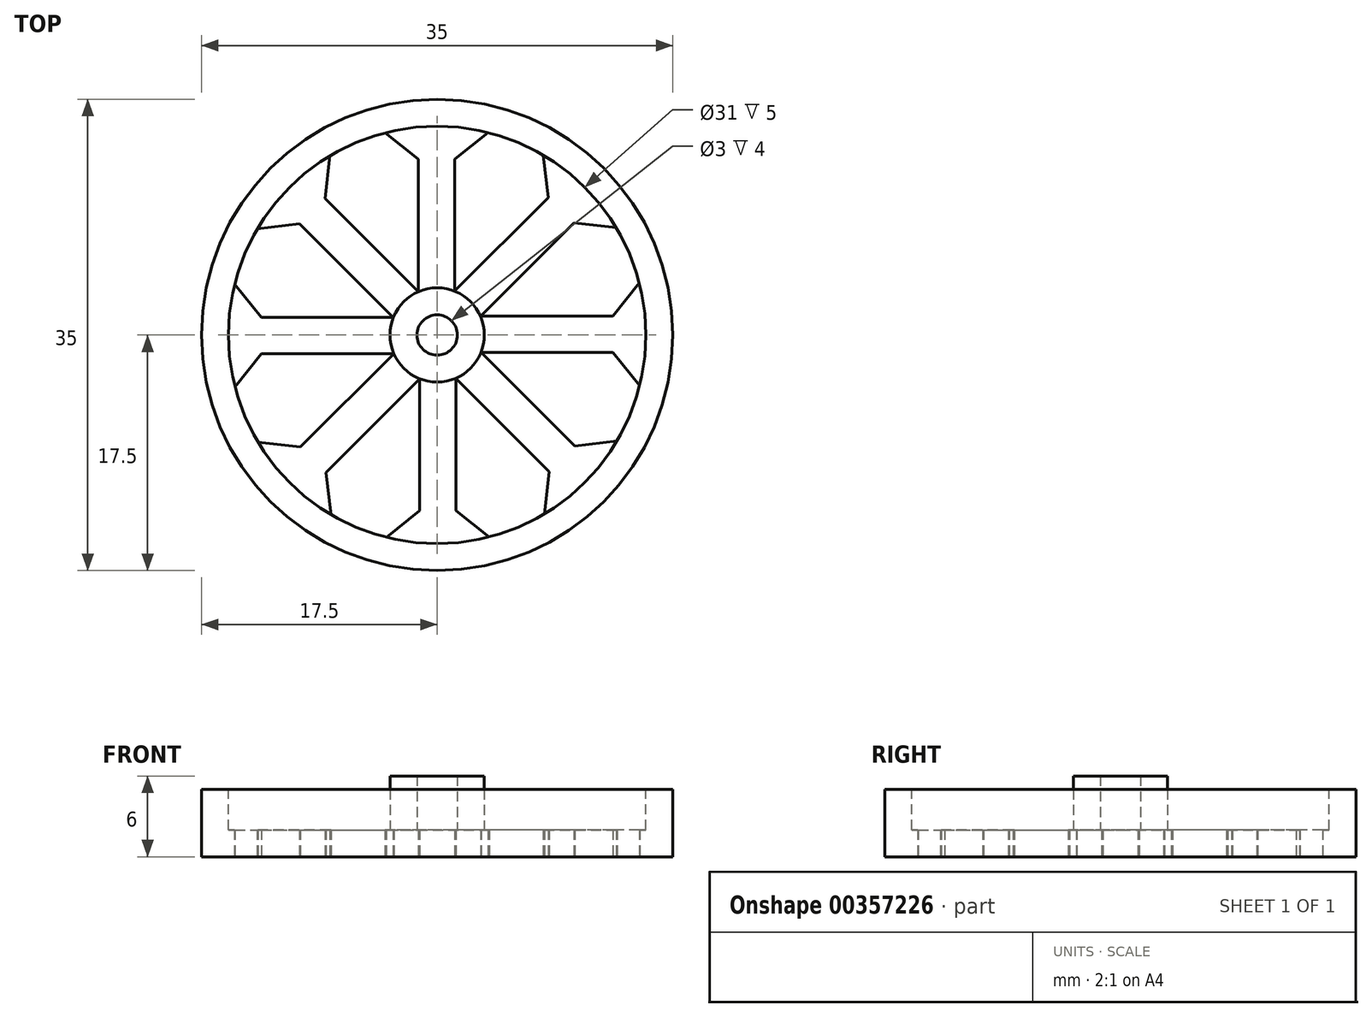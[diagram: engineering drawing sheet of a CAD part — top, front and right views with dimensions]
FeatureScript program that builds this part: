
annotation { "Feature Type Name" : "Feature", "Feature Type Description" : "" }
export const myFeature = defineFeature(function(context is Context, id is Id, definition is map)
    precondition{}
    {
        {
            var Q0;
            Q0=qCreatedBy(makeId("Top.planeOp"),FACE);
            var sketch = newSketch(context, id + "F0", { "sketchPlane" : qUnion([Q0])});
            skCircle(sketch, "E0", {"center": v(0, 0) * mm, "radius": 17.5 * mm});
            skSolve(sketch);
        }
        {
            var Q0;
            Q0=makeQuery(id+"F0.imprint","IMPRINT",FACE,{"disambiguationData":[TD([[makeQuery(id+"F0.imprint","IMPRINT",EDGE,{"derivedFrom":sQuery(id+"F0.wireOp",EDGE,"E0")}),1.0]])]});
            extrude(context, id + "F1", {"entities" : qUnion([Q0]), "depth" : 5 * mm});
        }
        {
            var Q0;
            Q0=makeQuery(id+"F1.opExtrude","CAP_FACE",FACE,{"disambiguationData":[OSD([sQuery(id+"F0.wireOp",EDGE,"E0")])],"isStart":false});
            var sketch = newSketch(context, id + "F2", { "sketchPlane" : qUnion([Q0])});
            skCircle(sketch, "E1", {"center": v(0, 0) * mm, "radius": 15.5 * mm});
            skSolve(sketch);
        }
        {
            var Q0;
            Q0 = qSketchRegion(id + "F2", true);
            extrude(context, id + "F3", {"entities" : qUnion([Q0]), "operationType" : NewBodyOperationType.REMOVE, "oppositeDirection" : true, "depth" : 3 * mm});
        }
        {
            var Q0;
            Q0=qCreatedBy(makeId("Top.planeOp"),FACE);
            var sketch = newSketch(context, id + "F4", { "sketchPlane" : qUnion([Q0])});
            skCircle(sketch, "E2", {"center": v(0, 0) * mm, "radius": 1.5 * mm});
            skCircle(sketch, "E3", {"center": v(0, 0) * mm, "radius": 3.5 * mm});
            skSolve(sketch);
        }
        {
            var Q0;
            Q0 = qSketchRegion(id + "F4", true);
            extrude(context, id + "F5", {"entities" : qUnion([Q0]), "operationType" : NewBodyOperationType.ADD, "depth" : 6 * mm});
        }
        {
            var Q0;
            Q0=makeQuery(id+"F1.opExtrude","CAP_FACE",FACE,{"disambiguationData":[OSD([sQuery(id+"F0.wireOp",EDGE,"E0")])],"isStart":true});
            var sketch = newSketch(context, id + "F6", { "sketchPlane" : qUnion([Q0])});
            skCircle(sketch, "E4", {"center": v(0, 0) * mm, "radius": 15.5 * mm});
            skSolve(sketch);
        }
        {
            var Q0;
            Q0=makeQuery(id+"F6.imprint","IMPRINT",FACE,{"disambiguationData":[TD([[makeQuery(id+"F6.imprint","IMPRINT",EDGE,{"derivedFrom":sQuery(id+"F6.wireOp",EDGE,"E4")}),1.0]])]});
            var sketch = newSketch(context, id + "F7", { "sketchPlane" : qUnion([Q0])});
            skLineSegment(sketch, "E5", {"start": v(-1.3, 2.05) * mm, "end": v(-1.3, 13.05) * mm});
            skLineSegment(sketch, "E6", {"start": v(1.39, 2.05) * mm, "end": v(1.39, 13.05) * mm});
            skLineSegment(sketch, "E7", {"start": v(1.39, 13.05) * mm, "end": v(4.83, 15.76) * mm});
            skLineSegment(sketch, "E8", {"start": v(-1.3, 13.05) * mm, "end": v(-4.67, 15.76) * mm});
            skLineSegment(sketch, "E9.1.0", {"start": v(-2.37, 0.53) * mm, "end": v(-10.15, 8.3) * mm});
            skLineSegment(sketch, "E9.1.1", {"start": v(-10.15, 8.3) * mm, "end": v(-14.45, 7.84) * mm});
            skLineSegment(sketch, "E9.1.2", {"start": v(-8.25, 10.2) * mm, "end": v(-7.72, 14.56) * mm});
            skLineSegment(sketch, "E9.1.3", {"start": v(-0.47, 2.43) * mm, "end": v(-8.25, 10.2) * mm});
            skLineSegment(sketch, "E9.2.0", {"start": v(-2.05, -1.3) * mm, "end": v(-13.05, -1.3) * mm});
            skLineSegment(sketch, "E9.2.1", {"start": v(-13.05, -1.3) * mm, "end": v(-15.76, -4.67) * mm});
            skLineSegment(sketch, "E9.2.2", {"start": v(-13.05, 1.39) * mm, "end": v(-15.76, 4.83) * mm});
            skLineSegment(sketch, "E9.2.3", {"start": v(-2.05, 1.39) * mm, "end": v(-13.05, 1.39) * mm});
            skLineSegment(sketch, "E9.3.0", {"start": v(-0.53, -2.37) * mm, "end": v(-8.3, -10.15) * mm});
            skLineSegment(sketch, "E9.3.1", {"start": v(-8.3, -10.15) * mm, "end": v(-7.84, -14.45) * mm});
            skLineSegment(sketch, "E9.3.2", {"start": v(-10.2, -8.25) * mm, "end": v(-14.56, -7.72) * mm});
            skLineSegment(sketch, "E9.3.3", {"start": v(-2.43, -0.47) * mm, "end": v(-10.2, -8.25) * mm});
            skLineSegment(sketch, "E9.4.0", {"start": v(1.3, -2.05) * mm, "end": v(1.3, -13.05) * mm});
            skLineSegment(sketch, "E9.4.1", {"start": v(1.3, -13.05) * mm, "end": v(4.67, -15.76) * mm});
            skLineSegment(sketch, "E9.4.2", {"start": v(-1.39, -13.05) * mm, "end": v(-4.83, -15.76) * mm});
            skLineSegment(sketch, "E9.4.3", {"start": v(-1.39, -2.05) * mm, "end": v(-1.39, -13.05) * mm});
            skLineSegment(sketch, "E9.5.0", {"start": v(2.37, -0.53) * mm, "end": v(10.15, -8.3) * mm});
            skLineSegment(sketch, "E9.5.1", {"start": v(10.15, -8.3) * mm, "end": v(14.45, -7.84) * mm});
            skLineSegment(sketch, "E9.5.2", {"start": v(8.25, -10.2) * mm, "end": v(7.72, -14.56) * mm});
            skLineSegment(sketch, "E9.5.3", {"start": v(0.47, -2.43) * mm, "end": v(8.25, -10.2) * mm});
            skLineSegment(sketch, "E9.6.0", {"start": v(2.05, 1.3) * mm, "end": v(13.05, 1.3) * mm});
            skLineSegment(sketch, "E9.6.1", {"start": v(13.05, 1.3) * mm, "end": v(15.76, 4.67) * mm});
            skLineSegment(sketch, "E9.6.2", {"start": v(13.05, -1.39) * mm, "end": v(15.76, -4.83) * mm});
            skLineSegment(sketch, "E9.6.3", {"start": v(2.05, -1.39) * mm, "end": v(13.05, -1.39) * mm});
            skLineSegment(sketch, "E9.7.0", {"start": v(0.53, 2.37) * mm, "end": v(8.3, 10.15) * mm});
            skLineSegment(sketch, "E9.7.1", {"start": v(8.3, 10.15) * mm, "end": v(7.84, 14.45) * mm});
            skLineSegment(sketch, "E9.7.2", {"start": v(10.2, 8.25) * mm, "end": v(14.56, 7.72) * mm});
            skLineSegment(sketch, "E9.7.3", {"start": v(2.43, 0.47) * mm, "end": v(10.2, 8.25) * mm});
            skPoint(sketch, "E9.center", {"position": v(0, 0) * mm});
            skSolve(sketch);
        }
        {
            var Q0;
            {var subQ3=sQuery(id+"F7.wireOp",EDGE,"E9.2.0");var subQ7=sQuery(id+"F7.wireOp",EDGE,"E9.2.1");var subQ8=makeQuery(id+"F7.imprint","INTERSECT",VERTEX,{"derivedFrom":[subQ3,subQ7]});Q0=makeQuery(id+"F7.imprint","IMPRINT",FACE,{"disambiguationData":[TD([[makeQuery(id+"F7.imprint","IMPRINT",EDGE,{"disambiguationData":[TD([[subQ8,1.0]])],"derivedFrom":subQ3}),1.0]])]});}
            var Q1;
            {var subQ3=sQuery(id+"F7.wireOp",EDGE,"E9.1.0");var subQ7=sQuery(id+"F7.wireOp",EDGE,"E9.1.1");var subQ8=makeQuery(id+"F7.imprint","INTERSECT",VERTEX,{"derivedFrom":[subQ3,subQ7]});Q1=makeQuery(id+"F7.imprint","IMPRINT",FACE,{"disambiguationData":[TD([[makeQuery(id+"F7.imprint","IMPRINT",EDGE,{"disambiguationData":[TD([[subQ8,1.0]])],"derivedFrom":subQ3}),1.0]])]});}
            var Q2;
            {var subQ3=sQuery(id+"F7.wireOp",EDGE,"E5");var subQ7=sQuery(id+"F7.wireOp",EDGE,"E8");var subQ8=makeQuery(id+"F7.imprint","INTERSECT",VERTEX,{"derivedFrom":[subQ3,subQ7]});Q2=makeQuery(id+"F7.imprint","IMPRINT",FACE,{"disambiguationData":[TD([[makeQuery(id+"F7.imprint","IMPRINT",EDGE,{"disambiguationData":[TD([[subQ8,1.0]])],"derivedFrom":subQ3}),1.0]])]});}
            var Q3;
            {var subQ5=sQuery(id+"F7.wireOp",EDGE,"E6");var subQ7=sQuery(id+"F7.wireOp",EDGE,"E7");var subQ8=makeQuery(id+"F7.imprint","INTERSECT",VERTEX,{"derivedFrom":[subQ5,subQ7]});Q3=makeQuery(id+"F7.imprint","IMPRINT",FACE,{"disambiguationData":[TD([[makeQuery(id+"F7.imprint","IMPRINT",EDGE,{"disambiguationData":[TD([[subQ8,1.0]])],"derivedFrom":subQ5}),-1.0]])]});}
            var Q4;
            {var subQ3=sQuery(id+"F7.wireOp",EDGE,"E9.6.0");var subQ7=sQuery(id+"F7.wireOp",EDGE,"E9.6.1");var subQ8=makeQuery(id+"F7.imprint","INTERSECT",VERTEX,{"derivedFrom":[subQ3,subQ7]});Q4=makeQuery(id+"F7.imprint","IMPRINT",FACE,{"disambiguationData":[TD([[makeQuery(id+"F7.imprint","IMPRINT",EDGE,{"disambiguationData":[TD([[subQ8,1.0]])],"derivedFrom":subQ3}),1.0]])]});}
            var Q5;
            {var subQ3=sQuery(id+"F7.wireOp",EDGE,"E9.5.0");var subQ7=sQuery(id+"F7.wireOp",EDGE,"E9.5.1");var subQ8=makeQuery(id+"F7.imprint","INTERSECT",VERTEX,{"derivedFrom":[subQ3,subQ7]});Q5=makeQuery(id+"F7.imprint","IMPRINT",FACE,{"disambiguationData":[TD([[makeQuery(id+"F7.imprint","IMPRINT",EDGE,{"disambiguationData":[TD([[subQ8,1.0]])],"derivedFrom":subQ3}),1.0]])]});}
            var Q6;
            {var subQ3=sQuery(id+"F7.wireOp",EDGE,"E9.4.0");var subQ7=sQuery(id+"F7.wireOp",EDGE,"E9.4.1");var subQ8=makeQuery(id+"F7.imprint","INTERSECT",VERTEX,{"derivedFrom":[subQ3,subQ7]});Q6=makeQuery(id+"F7.imprint","IMPRINT",FACE,{"disambiguationData":[TD([[makeQuery(id+"F7.imprint","IMPRINT",EDGE,{"disambiguationData":[TD([[subQ8,1.0]])],"derivedFrom":subQ3}),1.0]])]});}
            var Q7;
            {var subQ3=sQuery(id+"F7.wireOp",EDGE,"E9.3.0");var subQ7=sQuery(id+"F7.wireOp",EDGE,"E9.3.1");var subQ9=makeQuery(id+"F7.imprint","INTERSECT",VERTEX,{"derivedFrom":[subQ3,subQ7]});Q7=makeQuery(id+"F7.imprint","IMPRINT",FACE,{"disambiguationData":[TD([[makeQuery(id+"F7.imprint","IMPRINT",EDGE,{"disambiguationData":[TD([[subQ9,1.0]])],"derivedFrom":subQ3}),1.0]])]});}
            extrude(context, id + "F8", {"entities" : qUnion([Q0, Q1, Q2, Q3, Q4, Q5, Q6, Q7]), "operationType" : NewBodyOperationType.REMOVE, "oppositeDirection" : true, "depth" : 25 * mm});
        }
    });
